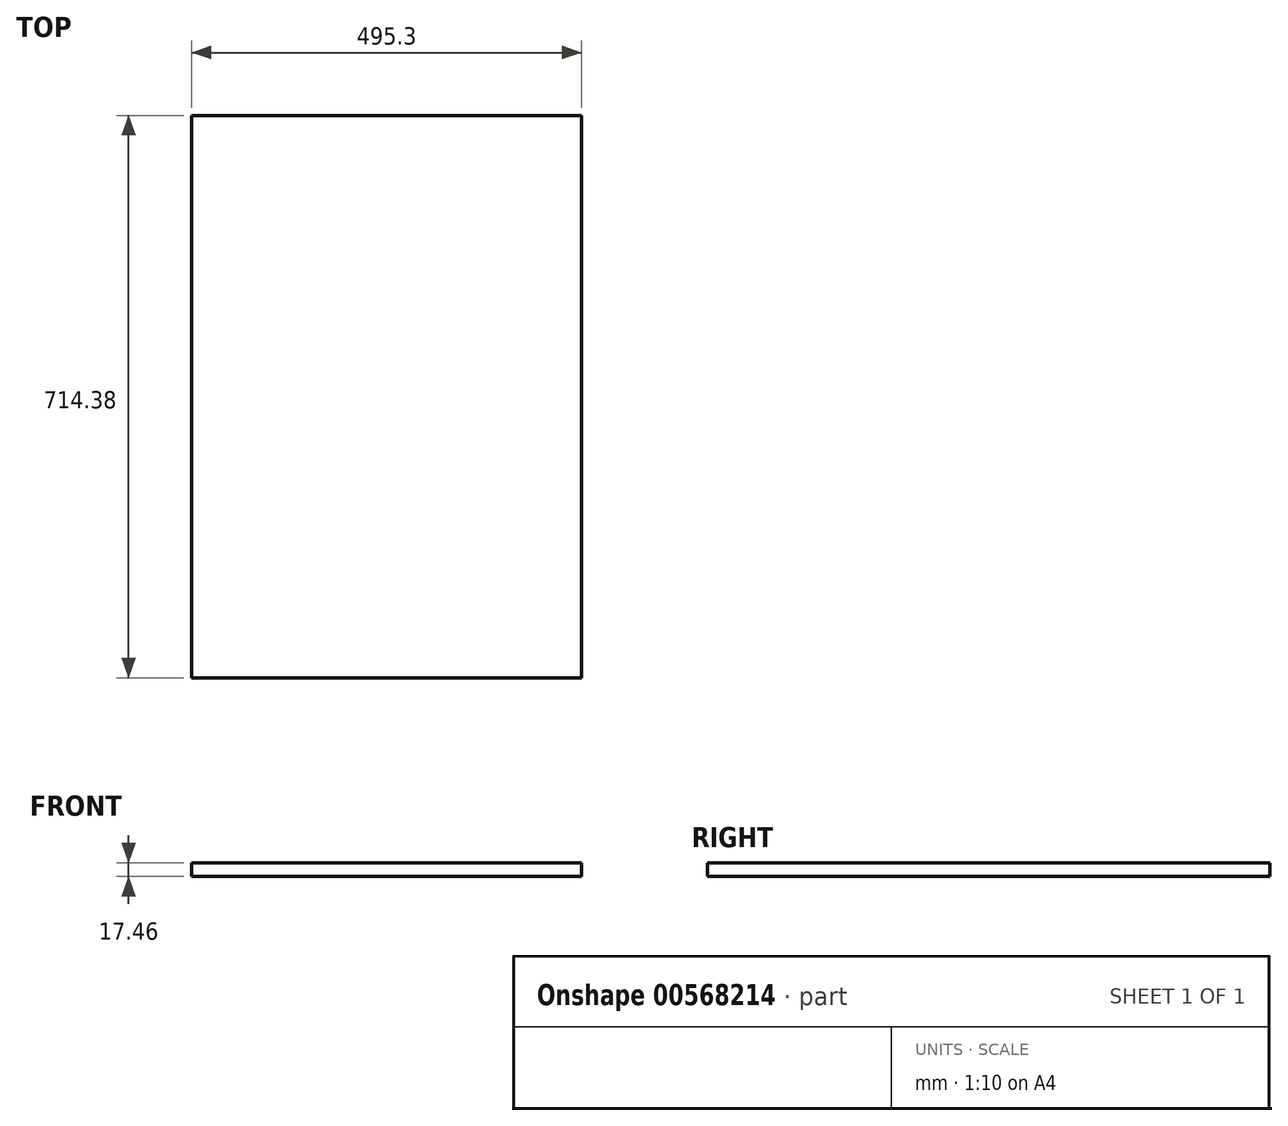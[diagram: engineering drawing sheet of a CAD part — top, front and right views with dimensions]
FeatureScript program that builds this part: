
annotation { "Feature Type Name" : "Feature", "Feature Type Description" : "" }
export const myFeature = defineFeature(function(context is Context, id is Id, definition is map)
    precondition{}
    {
        {
            var Q0;
            Q0=qCreatedBy(makeId("Top.planeOp"),FACE);
            var sketch = newSketch(context, id + "F0", { "sketchPlane" : qUnion([Q0])});
            skLineSegment(sketch, "E0.bottom", {"start": v(0, 0) * mm, "end": v(495.3, 0) * mm});
            skLineSegment(sketch, "E0.top", {"start": v(0, 714.38) * mm, "end": v(495.3, 714.38) * mm});
            skLineSegment(sketch, "E0.left", {"start": v(0, 0) * mm, "end": v(0, 714.38) * mm});
            skLineSegment(sketch, "E0.right", {"start": v(495.3, 0) * mm, "end": v(495.3, 714.38) * mm});
            skSolve(sketch);
        }
        {
            var Q0;
            Q0=makeQuery(id+"F0.imprint","IMPRINT",FACE,{"disambiguationData":[TD([[makeQuery(id+"F0.imprint","IMPRINT",EDGE,{"derivedFrom":sQuery(id+"F0.wireOp",EDGE,"E0.bottom")}),1.0]])]});
            extrude(context, id + "F1", {"entities" : qUnion([Q0]), "depth" : 17.46 * mm, "offsetDistance" : 25.4 * mm});
        }
    });
